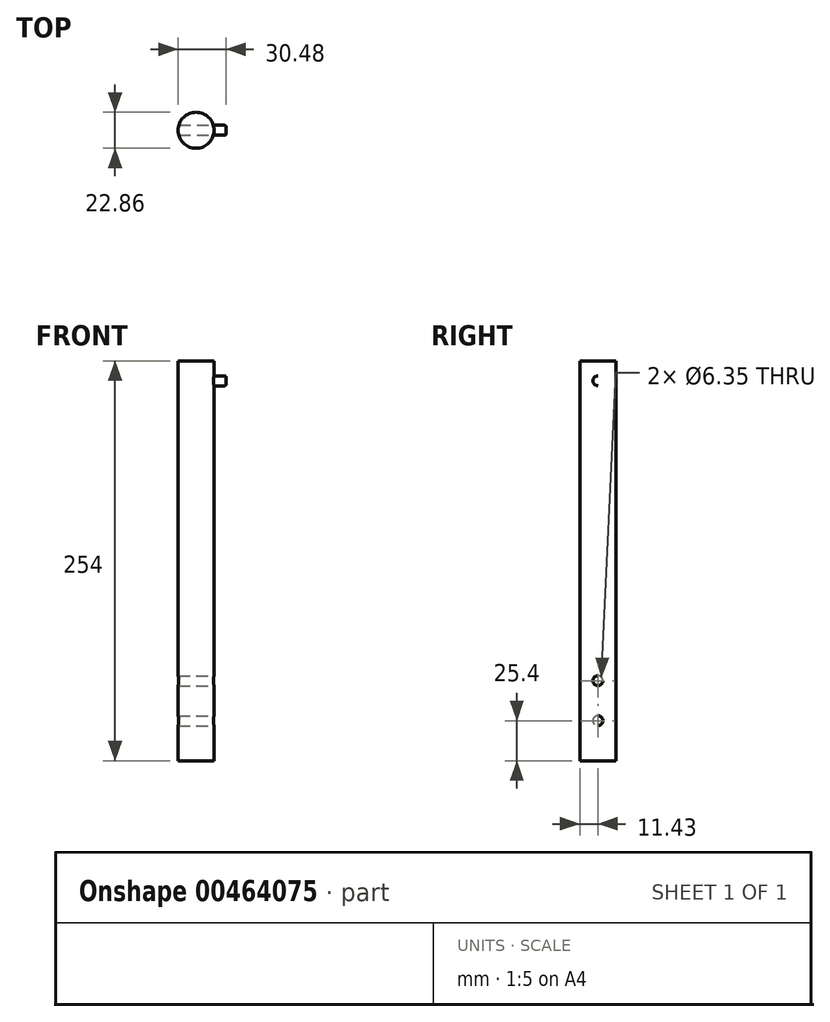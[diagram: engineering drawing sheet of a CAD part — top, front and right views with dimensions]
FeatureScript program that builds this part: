
annotation { "Feature Type Name" : "Feature", "Feature Type Description" : "" }
export const myFeature = defineFeature(function(context is Context, id is Id, definition is map)
    precondition{}
    {
        {
            var Q0;
            Q0=qCreatedBy(makeId("Top.planeOp"),FACE);
            var sketch = newSketch(context, id + "F0", { "sketchPlane" : qUnion([Q0])});
            skCircle(sketch, "E0", {"center": v(0, 0) * mm, "radius": 11.43 * mm});
            skSolve(sketch);
        }
        {
            var Q0;
            Q0 = qSketchRegion(id + "F0", true);
            extrude(context, id + "F1", {"entities" : qUnion([Q0]), "depth" : 254 * mm, "offsetDistance" : 25.4 * mm});
        }
        {
            var Q0;
            Q0=qCreatedBy(makeId("Right.planeOp"),FACE);
            var sketch = newSketch(context, id + "F2", { "sketchPlane" : qUnion([Q0])});
            skLineSegment(sketch, "E1", {"start": v(0, 0) * mm, "end": v(0, 25.4) * mm});
            skLineSegment(sketch, "E2", {"start": v(0, 25.4) * mm, "end": v(0, 50.8) * mm});
            skCircle(sketch, "E3", {"center": v(0, 25.4) * mm, "radius": 3.18 * mm});
            skCircle(sketch, "E4", {"center": v(0, 50.8) * mm, "radius": 3.18 * mm});
            skSolve(sketch);
        }
        {
            var Q0;
            Q0 = qSketchRegion(id + "F2", true);
            extrude(context, id + "F3", {"entities" : qUnion([Q0]), "operationType" : NewBodyOperationType.REMOVE, "oppositeDirection" : true, "depth" : 25.4 * mm, "offsetDistance" : 25.4 * mm, "hasSecondDirection" : true, "secondDirectionOppositeDirection" : false, "secondDirectionDepth" : 25.4 * mm});
        }
        {
            var Q0;
            Q0=qCreatedBy(makeId("Right.planeOp"),FACE);
            var sketch = newSketch(context, id + "F4", { "sketchPlane" : qUnion([Q0])});
            skLineSegment(sketch, "E5", {"start": v(0, 0) * mm, "end": v(0, 241.3) * mm});
            skCircle(sketch, "E6", {"center": v(0, 241.3) * mm, "radius": 3.18 * mm});
            skSolve(sketch);
        }
        {
            var Q0;
            Q0 = qSketchRegion(id + "F4", true);
            extrude(context, id + "F5", {"entities" : qUnion([Q0]), "operationType" : NewBodyOperationType.ADD, "depth" : 19.05 * mm, "offsetDistance" : 25.4 * mm});
        }
        {
            var Q0;
            Q0=makeQuery(id+"F5.opExtrude","CAP_EDGE",EDGE,{"disambiguationData":[OSD([sQuery(id+"F4.wireOp",EDGE,"E6")])],"isStart":false});
            fillet(context, id + "F6", {"entities" : qUnion([Q0]), "radius" : 1.27 * mm, "tangentPropagation" : true, "rho" : 0.5, "crossSection" : FilletCrossSection.CONIC, "allowEdgeOverflow" : false});
        }
    });
